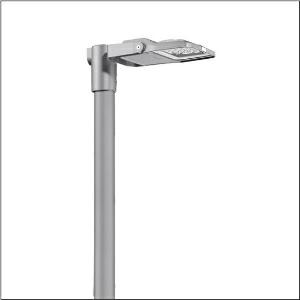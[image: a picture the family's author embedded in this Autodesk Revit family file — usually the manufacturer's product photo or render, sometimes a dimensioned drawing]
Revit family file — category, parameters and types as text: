
# Revit family: floodlight_fl_21_iq_micro___pl61_5xa7762a4c3a_196d
name_source: partatom
category: Lighting Fixtures
units: mm (PartAtom-declared; Revit-internal decimal feet)

## family parameters
Cut with Voids When Loaded = No
Host = Face
Light Source = No
Part Type = Normal
Room Calculation Point = No
Round Connector Dimension = Use Diameter
Shared = No

## types (1)
- --- (1 x LED, 3030 lm, 23.1 W, 4000K)
    Apparent Load = 23 VA
    CIE Flux Codes = 33 65 98 100 100
    Color Rendering = 70
    Color Temperature = 4000K
    Default Elevation = 1800 mm
    Description = Floodlight FL 21 iQ micro, floodlight, primary light control with lens, of PMMA, primary optical cover: protective disc, of toughened safety glass, transparent, light distribution: PL61, light emission: direct distribution, installation type: surface-mounted, LED, High Power LED, rated luminous flux: 3.030lm, luminous efficacy: 131lm/W, light colour: 740, colour temperature: 4000K, control: Auto-Match, Temp-Guard, Night-Set, Smart-Wire, Desk-Remote (wireless, voltage-free reading and setting of iQ features in the workshop via application-optimized NFC function/RFID function), optimised constant luminous flux control (CLO 2.0), Street-Remote, with terminal, 6-pole, mains connection: 220..240V, AC, 50/60Hz, start of lifetime: 23W, end of service life: 24W, reduction: 11W, luminaire housing, of diecast aluminium, powder-coated, Siteco® metallic grey (DB 702S), corrosivity category C5 mid according to DIN EN ISO 12944, sealing non-destructively replaceable, please order mast flange separately, mast bracket, of steel, galvanised, powder-coated, Siteco® metallic grey (DB 702S), protection rating (complete): IP66, insulation class (complete): insulation class II (safety insulation), certification: CE, ENEC, VDE, protection symbol: D, impact resistance: IK07, permissible operating ambient temperature: -40..+40°C, permissible operating ambient temperature for outdoor applications: -40..+50°C, standard: DIN EN 12944, LABS conformity tested according to VDMA 24364:2018-05, packaging unit: 1 piece

Light Distribution: PL61
    Height = 65 mm
    Lamp = 1 x LED
    Lamp Light Flux = 3030 lm
    Lamp Power = 23.1 W
    Lamp count = 1
    Length = 312 mm
    Luminous efficacy = 131 lm/W
    Manufacturer = Siteco
    ModVariant = No
    Model = 5XA7762A4C3A
    Number of Poles = 1
    OnlyDefault = Yes
    Power Factor = 1
    Product Name = Floodlight FL 21 iQ micro | PL61
    Product group = floodlight | pylon annexe
    ProductGroupID = 6200
    Protection Class = Protection class II
    Protection Degree = IP 66
    RLX_Detail_Level = 1
    RLX_Emergency_Light_Flux = 0 lm
    RLX_Emergency_Type = 0
    RLX_Emergency_Type_DB = No
    RlxData = <blob elided: 101785 chars, md5=5817a665>
    Socket = socket
    Standby Power = 0 W
    System Light Flux = 3030 lm
    System Power = 23 W
    Type Comments = factory setting: luminous flux: 100 % | dim-lin: 254 | 455 mA
    Type Image = l_1007121.jpg
    URL = http://relux.com
    VarID = @adj_128767
    Voltage = 0 V
    Weight = 0.00 kg
    Width = 230 mm

## geometry (parser evidence)
native form markers: Blend x4, Sweep x11
no freeform markers — native parametric forms only
